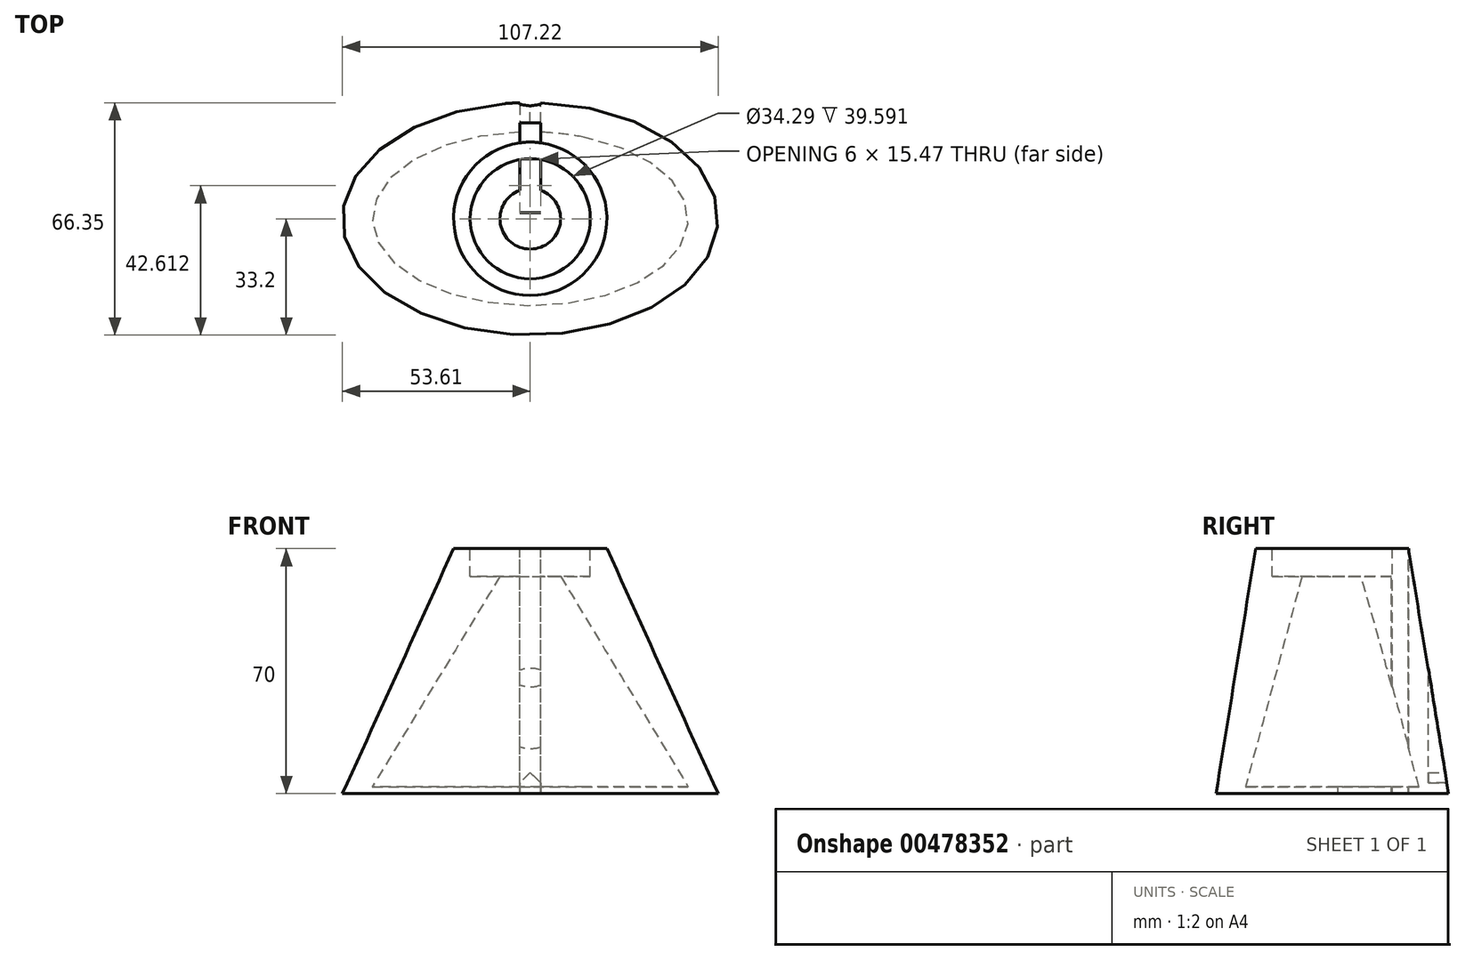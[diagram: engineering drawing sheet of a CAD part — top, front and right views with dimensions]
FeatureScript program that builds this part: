
annotation { "Feature Type Name" : "Feature", "Feature Type Description" : "" }
export const myFeature = defineFeature(function(context is Context, id is Id, definition is map)
    precondition{}
    {
        {
            var Q0;
            Q0=qCreatedBy(makeId("Top.planeOp"),FACE);
            var sketch = newSketch(context, id + "F0", { "sketchPlane" : qUnion([Q0])});
            skEllipse(sketch, "E0", {"center": v(0, 0) * mm, "majorRadius": 53.61 * mm, "minorRadius": 33.2 * mm, "majorAxis": v(-1, 0)});
            skSolve(sketch);
        }
        {
            var Q0;
            Q0=qCreatedBy(makeId("Top.planeOp"),FACE);
            cPlane(context, id + "F1", {"entities" : qUnion([Q0]), "cplaneType" : CPlaneType.OFFSET, "offset" : 70 * mm, "width" : 152.4 * mm, "height" : 152.4 * mm});
        }
        {
            var Q0;
            Q0=qCreatedBy(makeId("Top.planeOp"),FACE);
            cPlane(context, id + "F2", {"entities" : qUnion([Q0]), "cplaneType" : CPlaneType.OFFSET, "offset" : 2 * mm, "width" : 150 * mm, "height" : 150 * mm});
        }
        {
            var Q0;
            Q0=qCreatedBy(id+"F1.planeOp",FACE);
            var sketch = newSketch(context, id + "F3", { "sketchPlane" : qUnion([Q0])});
            skCircle(sketch, "E1", {"center": v(0, 0) * mm, "radius": 21.88 * mm});
            skSolve(sketch);
        }
        {
            var Q0;
            Q0=makeQuery(id+"F0.imprint","IMPRINT",FACE,{"disambiguationData":[TD([[makeQuery(id+"F0.imprint","IMPRINT",EDGE,{"derivedFrom":sQuery(id+"F0.wireOp",EDGE,"E0")}),1.0]])]});
            var Q1;
            Q1=makeQuery(id+"F3.imprint","IMPRINT",FACE,{"disambiguationData":[TD([[makeQuery(id+"F3.imprint","IMPRINT",EDGE,{"derivedFrom":sQuery(id+"F3.wireOp",EDGE,"E1")}),1.0]])]});
            loft(context, id + "F4", {"sheetProfilesArray" : [{ "sheetProfileEntities" : qUnion([Q0]) }, { "sheetProfileEntities" : qUnion([Q1]) }]});
        }
        {
            var Q0;
            Q0=makeQuery(id+"F4.opLoft","CAP_FACE",FACE,{"disambiguationData":[OSD([makeQuery(id+"F3.imprint","IMPRINT",FACE,{"disambiguationData":[TD([[makeQuery(id+"F3.imprint","IMPRINT",EDGE,{"derivedFrom":sQuery(id+"F3.wireOp",EDGE,"E1")}),1.0]])]})])],"isStart":true});
            var sketch = newSketch(context, id + "F5", { "sketchPlane" : qUnion([Q0])});
            skCircle(sketch, "E2", {"center": v(0, 0) * mm, "radius": 17.14 * mm});
            skSolve(sketch);
        }
        {
            var Q0;
            Q0=makeQuery(id+"F5.imprint","IMPRINT",FACE,{"disambiguationData":[TD([[makeQuery(id+"F5.imprint","IMPRINT",EDGE,{"derivedFrom":sQuery(id+"F5.wireOp",EDGE,"E2")}),1.0]])]});
            var Q1;
            Q1=sQuery(id+"F5.wireOp",EDGE,"E2");
            extrude(context, id + "F6", {"entities" : qUnion([Q0]), "operationType" : NewBodyOperationType.REMOVE, "surfaceEntities" : qUnion([Q1]), "oppositeDirection" : true, "depth" : 8 * mm});
        }
        {
            var Q0;
            Q0=qCreatedBy(id+"F2.planeOp",FACE);
            var sketch = newSketch(context, id + "F7", { "sketchPlane" : qUnion([Q0])});
            skEllipse(sketch, "E3", {"center": v(0, 0) * mm, "majorRadius": 45.08 * mm, "minorRadius": 24.78 * mm, "majorAxis": v(1, 0)});
            skSolve(sketch);
        }
        {
            var Q0;
            Q0=makeQuery(id+"F6.boolean.opBoolean","COPY",FACE,{"derivedFrom":makeQuery(id+"F6.opExtrude","CAP_FACE",FACE,{"disambiguationData":[OSD([sQuery(id+"F5.wireOp",EDGE,"E2")])],"isStart":false})});
            var sketch = newSketch(context, id + "F8", { "sketchPlane" : qUnion([Q0])});
            skCircle(sketch, "E4", {"center": v(0, 0) * mm, "radius": 8.66 * mm});
            skSolve(sketch);
        }
        {
            var Q0;
            Q0=qSketchRegion(id+"F7",true);
            var Q1;
            Q1=qSketchRegion(id+"F8",true);
            loft(context, id + "F9", {"operationType" : NewBodyOperationType.REMOVE, "sheetProfilesArray" : [{ "sheetProfileEntities" : qUnion([Q0]) }, { "sheetProfileEntities" : qUnion([Q1]) }]});
        }
        {
            var Q0;
            Q0=makeQuery(id+"F4.opLoft","CAP_FACE",FACE,{"disambiguationData":[OSD([makeQuery(id+"F3.imprint","IMPRINT",FACE,{"disambiguationData":[TD([[makeQuery(id+"F3.imprint","IMPRINT",EDGE,{"derivedFrom":sQuery(id+"F3.wireOp",EDGE,"E1")}),1.0]])]})])],"isStart":true});
            var sketch = newSketch(context, id + "F10", { "sketchPlane" : qUnion([Q0])});
            skLineSegment(sketch, "E5.rect.bottom", {"start": v(3, 27.4) * mm, "end": v(-3, 27.4) * mm});
            skLineSegment(sketch, "E5.rect.top", {"start": v(3, -12.6) * mm, "end": v(-3, -12.6) * mm});
            skLineSegment(sketch, "E5.rect.left", {"start": v(3, 27.4) * mm, "end": v(3, -12.6) * mm});
            skLineSegment(sketch, "E5.rect.right", {"start": v(-3, 27.4) * mm, "end": v(-3, -12.6) * mm});
            skPoint(sketch, "E5.rect.middle", {"position": v(0, 7.4) * mm});
            skLineSegment(sketch, "E6", {"start": v(-3, 1.68) * mm, "end": v(3, 1.68) * mm});
            skSolve(sketch);
        }
        {
            var Q0;
            {var subQ5=sQuery(id+"F10.wireOp",EDGE,"E5.rect.bottom");Q0=makeQuery(id+"F10.imprint","IMPRINT",FACE,{"disambiguationData":[TD([[makeQuery(id+"F10.imprint","IMPRINT",EDGE,{"derivedFrom":subQ5}),1.0]])]});}
            var Q1;
            {var subQ3=sQuery(id+"F10.wireOp",EDGE,"E5.rect.left");var subQ5=makeQuery(id+"F6.boolean.opBoolean","COPY",EDGE,{"derivedFrom":makeQuery(id+"F6.opExtrude","CAP_EDGE",EDGE,{"disambiguationData":[OSD([sQuery(id+"F5.wireOp",EDGE,"E2")])],"isStart":true})});var subQ7=makeQuery(id+"F10.imprint","INTERSECT",VERTEX,{"derivedFrom":[subQ5,subQ3]});Q1=makeQuery(id+"F10.imprint","IMPRINT",FACE,{"disambiguationData":[TD([[makeQuery(id+"F10.imprint","IMPRINT",EDGE,{"disambiguationData":[TD([[subQ7,-1.0]])],"derivedFrom":subQ5}),-1.0]])]});}
            var Q2;
            {var subQ5=sQuery(id+"F10.wireOp",EDGE,"E6");Q2=makeQuery(id+"F10.imprint","IMPRINT",FACE,{"disambiguationData":[TD([[makeQuery(id+"F10.imprint","IMPRINT",EDGE,{"derivedFrom":subQ5}),1.0]])]});}
            extrude(context, id + "F11", {"entities" : qUnion([Q0, Q1, Q2]), "operationType" : NewBodyOperationType.REMOVE, "endBound" : BoundingType.THROUGH_ALL, "oppositeDirection" : true, "depth" : 60 * mm});
        }
        {
            var Q0;
            {var subQ0=sQuery(id+"F10.wireOp",EDGE,"E5.rect.bottom");Q0=makeQuery(id+"FKyBt0pK8GL4Poo_1.boolean.opBoolean","MERGE",FACE,{"derivedFrom":[makeQuery(id+"F11.boolean.opBoolean","COPY",FACE,{"derivedFrom":makeQuery(id+"F11.opExtrude","SWEPT_FACE",FACE,{"disambiguationData":[OSD([subQ0])]})}),makeQuery(id+"FKyBt0pK8GL4Poo_1.opExtrude","SWEPT_FACE",FACE,{"disambiguationData":[OSD([subQ0])]})]});}
            var sketch = newSketch(context, id + "F12", { "sketchPlane" : qUnion([Q0])});
            skLineSegment(sketch, "E7.rect.bottom", {"start": v(3, 6.08) * mm, "end": v(-3, 6.08) * mm});
            skLineSegment(sketch, "E7.rect.top", {"start": v(3, -6.08) * mm, "end": v(-3, -6.08) * mm});
            skLineSegment(sketch, "E7.rect.left", {"start": v(3, 6.08) * mm, "end": v(3, -6.08) * mm});
            skLineSegment(sketch, "E7.rect.right", {"start": v(-3, 6.08) * mm, "end": v(-3, -6.08) * mm});
            skPoint(sketch, "E7.rect.middle", {"position": v(0, 0) * mm});
            skSolve(sketch);
        }
        {
            var Q0;
            {var subQ4=sQuery(id+"F12.wireOp",EDGE,"E7.rect.bottom");Q0=makeQuery(id+"F12.imprint","IMPRINT",FACE,{"disambiguationData":[TD([[makeQuery(id+"F12.imprint","IMPRINT",EDGE,{"derivedFrom":subQ4}),1.0]])]});}
            extrude(context, id + "F13", {"entities" : qUnion([Q0]), "operationType" : NewBodyOperationType.REMOVE, "oppositeDirection" : true, "depth" : 25 * mm});
        }
        {
            var Q0;
            Q0=makeQuery(id+"F13.boolean.opBoolean","COPY",EDGE,{"derivedFrom":makeQuery(id+"F13.opExtrude","SWEPT_EDGE",EDGE,{"disambiguationData":[OSD([sQuery(id+"F10.wireOp",EDGE,"E5.rect.bottom"),sQuery(id+"F10.wireOp",EDGE,"E5.rect.left"),sQuery(id+"F12.wireOp",EDGE,"E7.rect.bottom"),sQuery(id+"F12.wireOp",EDGE,"E7.rect.left")])]})});
            var Q1;
            Q1=makeQuery(id+"F13.boolean.opBoolean","COPY",EDGE,{"derivedFrom":makeQuery(id+"F13.opExtrude","SWEPT_EDGE",EDGE,{"disambiguationData":[OSD([sQuery(id+"F10.wireOp",EDGE,"E5.rect.bottom"),sQuery(id+"F10.wireOp",EDGE,"E5.rect.right"),sQuery(id+"F12.wireOp",EDGE,"E7.rect.bottom"),sQuery(id+"F12.wireOp",EDGE,"E7.rect.right")])]})});
            chamfer(context, id + "F14", {"entities" : qUnion([Q0, Q1]), "width" : 3 * mm, "tangentPropagation" : true});
        }
        {
            var Q0;
            Q0=makeQuery(id+"F4.opLoft","CAP_FACE",FACE,{"disambiguationData":[OSD([makeQuery(id+"F3.imprint","IMPRINT",FACE,{"disambiguationData":[TD([[makeQuery(id+"F3.imprint","IMPRINT",EDGE,{"derivedFrom":sQuery(id+"F3.wireOp",EDGE,"E1")}),1.0]])]})])],"isStart":true});
            var sketch = newSketch(context, id + "F15", { "sketchPlane" : qUnion([Q0])});
            skCircle(sketch, "E8.cCircle", {"center": v(0, 0) * mm, "radius": 17.14 * mm, "construction": true});
            skLineSegment(sketch, "E8.0", {"start": v(9.9, -17.14) * mm, "end": v(-9.9, -17.14) * mm});
            skLineSegment(sketch, "E8.1", {"start": v(-9.9, -17.15) * mm, "end": v(-19.8, 0) * mm});
            skLineSegment(sketch, "E8.2", {"start": v(-19.8, 0) * mm, "end": v(-9.9, 17.14) * mm});
            skLineSegment(sketch, "E8.3", {"start": v(-9.9, 17.14) * mm, "end": v(9.9, 17.15) * mm});
            skLineSegment(sketch, "E8.4", {"start": v(9.9, 17.15) * mm, "end": v(19.8, 0) * mm});
            skLineSegment(sketch, "E8.5", {"start": v(19.8, 0) * mm, "end": v(9.9, -17.14) * mm});
            skPoint(sketch, "E8.0.midPoint", {"position": v(0, -17.14) * mm});
            skSolve(sketch);
        }
        {
            var Q0;
            {var subQ0=makeQuery(id+"F6.boolean.opBoolean","COPY",EDGE,{"derivedFrom":makeQuery(id+"F6.opExtrude","CAP_EDGE",EDGE,{"disambiguationData":[OSD([sQuery(id+"F5.wireOp",EDGE,"E2")])],"isStart":true})});var subQ1=sQuery(id+"F15.wireOp",EDGE,"E8.0");var subQ3=makeQuery(id+"F15.imprint","INTERSECT",VERTEX,{"disambiguationData":[OD(0.0)],"derivedFrom":[subQ0,subQ1]});Q0=makeQuery(id+"F15.imprint","IMPRINT",FACE,{"disambiguationData":[TD([[makeQuery(id+"F15.imprint","IMPRINT",EDGE,{"disambiguationData":[TD([[subQ3,-1.0]])],"derivedFrom":subQ1}),1.0]])]});}
            extrude(context, id + "F16", {"entities" : qUnion([Q0]), "operationType" : NewBodyOperationType.ADD, "oppositeDirection" : true, "depth" : 2 * mm});
        }
    });
